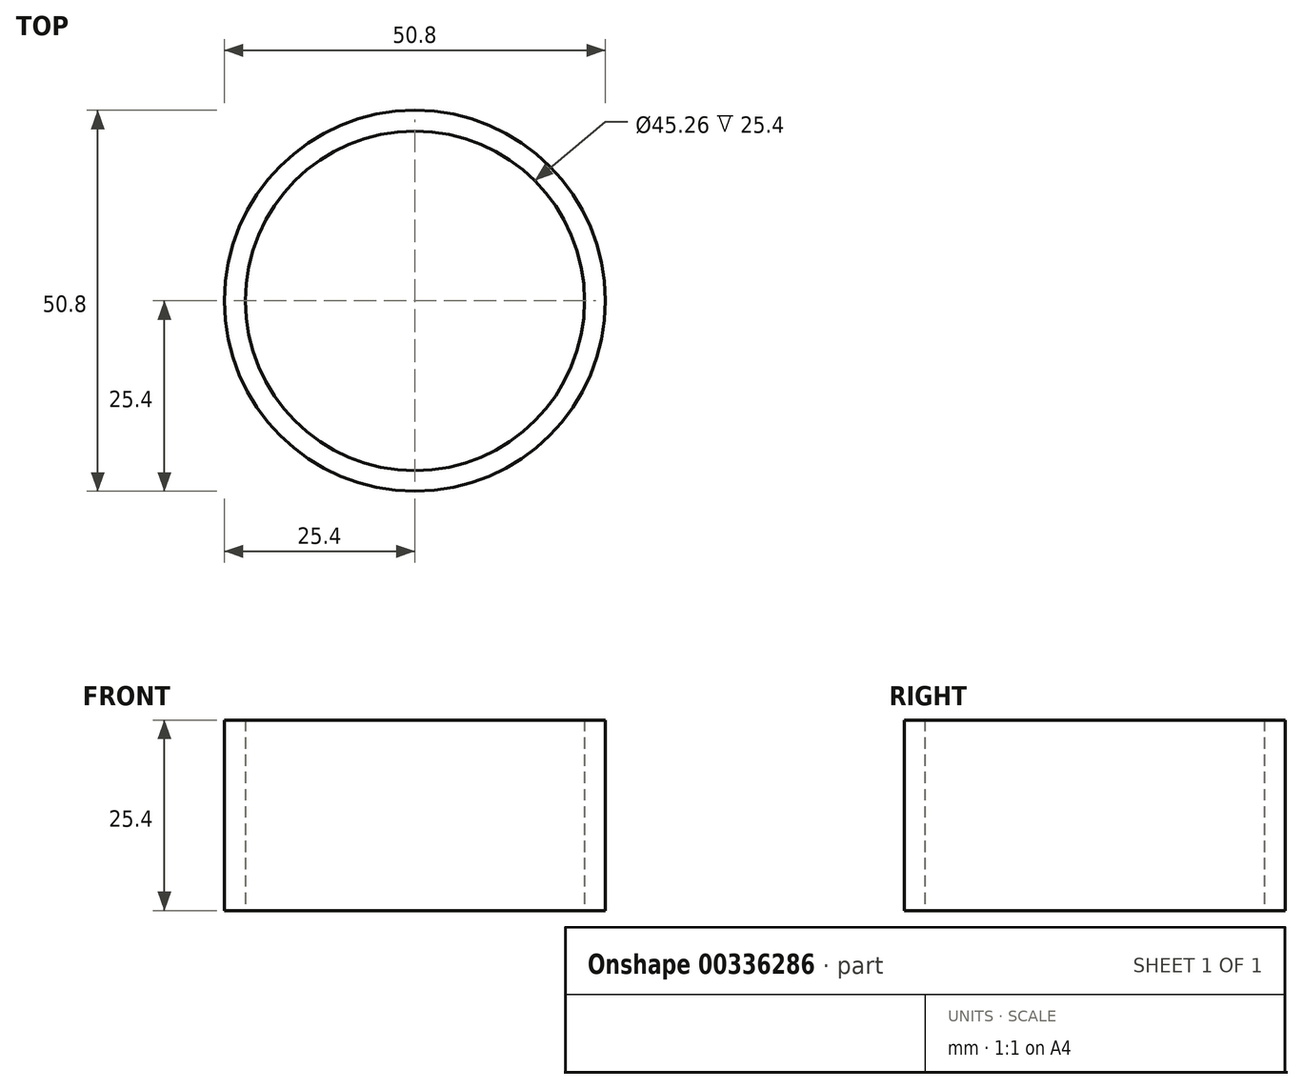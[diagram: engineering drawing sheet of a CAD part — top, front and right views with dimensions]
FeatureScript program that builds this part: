
annotation { "Feature Type Name" : "Feature", "Feature Type Description" : "" }
export const myFeature = defineFeature(function(context is Context, id is Id, definition is map)
    precondition{}
    {
        {
            var Q0;
            Q0=qCreatedBy(makeId("Top.planeOp"),FACE);
            var sketch = newSketch(context, id + "F0", { "sketchPlane" : qUnion([Q0])});
            skCircle(sketch, "E0", {"center": v(0, 0) * mm, "radius": 25.4 * mm});
            skCircle(sketch, "E1", {"center": v(0, 0) * mm, "radius": 22.63 * mm});
            skSolve(sketch);
        }
        {
            var Q0;
            Q0=makeQuery(id+"F0.imprint","IMPRINT",FACE,{"disambiguationData":[TD([[makeQuery(id+"F0.imprint","IMPRINT",EDGE,{"derivedFrom":sQuery(id+"F0.wireOp",EDGE,"E0")}),1.0]])]});
            extrude(context, id + "F1", {"entities" : qUnion([Q0]), "depth" : 25.4 * mm});
        }
    });
